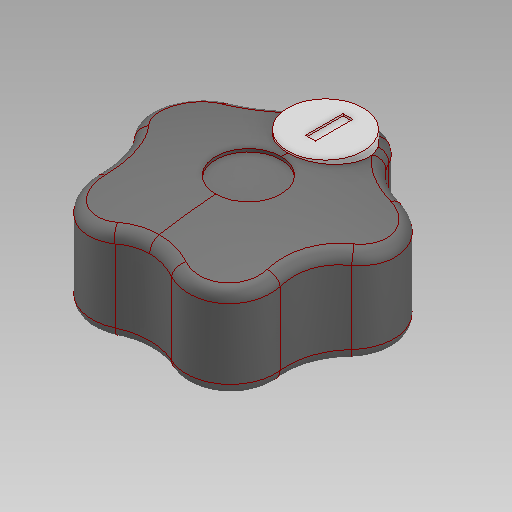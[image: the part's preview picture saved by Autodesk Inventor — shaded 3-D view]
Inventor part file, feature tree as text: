
AUTODESK INVENTOR PART (.ipt)
format: ipt  version: 2021 (Build 250183000, 183)  size: 415,232 bytes
history: native  units: in
note: dims shown in document units (in); Inventor stores cm internally (conversion verified against a paired STEP export)
features: fillet x1
ambient origin geometry x8: Origin, YZ Plane, XZ Plane, XY Plane, X Axis, Y Axis, Z Axis, Center Point
bodies: Solid1 (feature_tree)
feature tree (1):
  fillet  "Fillet3"  [1 undecoded]
note: 1 required parameter value undecoded (feature->parameter linkage not recoverable at this tier; creation-order binding heuristic only, values carry confidence <= 0.55)
